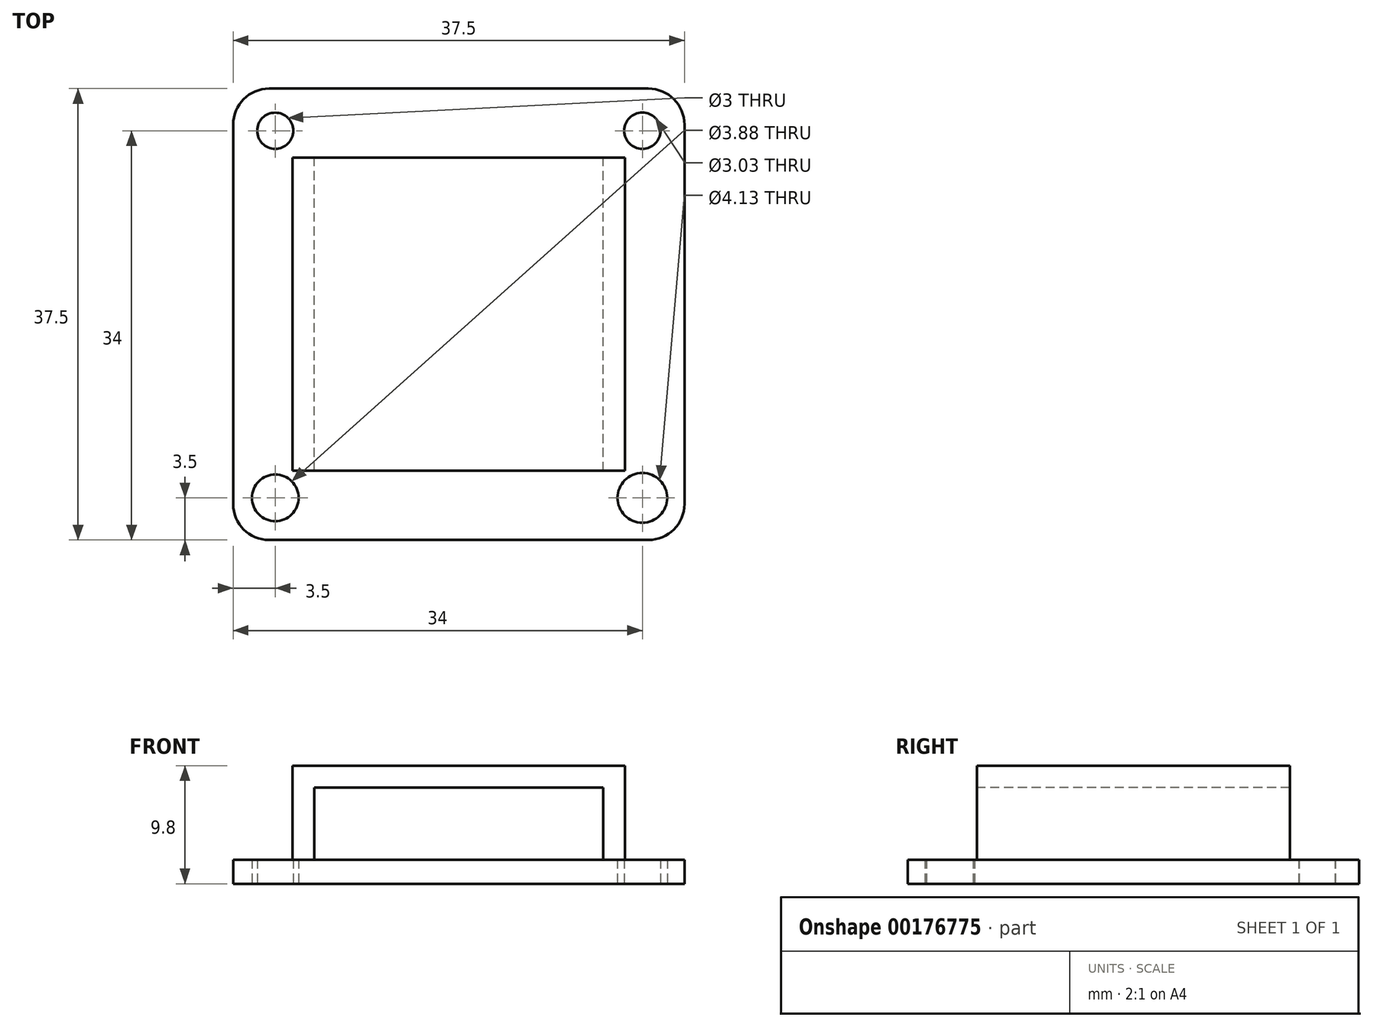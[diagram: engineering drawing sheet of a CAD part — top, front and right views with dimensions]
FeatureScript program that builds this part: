
annotation { "Feature Type Name" : "Feature", "Feature Type Description" : "" }
export const myFeature = defineFeature(function(context is Context, id is Id, definition is map)
    precondition{}
    {
        {
            var Q0;
            Q0=qCreatedBy(makeId("Top.planeOp"),FACE);
            var sketch = newSketch(context, id + "F0", { "sketchPlane" : qUnion([Q0])});
            skLineSegment(sketch, "E0.bottom", {"start": v(-15.75, 18.75) * mm, "end": v(15.75, 18.75) * mm});
            skLineSegment(sketch, "E0.top", {"start": v(-15.75, -18.75) * mm, "end": v(15.75, -18.75) * mm});
            skLineSegment(sketch, "E0.left", {"start": v(-18.75, 15.75) * mm, "end": v(-18.75, -15.75) * mm});
            skLineSegment(sketch, "E0.right", {"start": v(18.75, 15.75) * mm, "end": v(18.75, -15.75) * mm});
            skPoint(sketch, "E0.middle", {"position": v(0, 0) * mm});
            skLineSegment(sketch, "E1.bottom", {"start": v(-15.25, 15.25) * mm, "end": v(15.25, 15.25) * mm});
            skLineSegment(sketch, "E1.top", {"start": v(-15.25, -15.25) * mm, "end": v(15.25, -15.25) * mm});
            skLineSegment(sketch, "E1.left", {"start": v(-15.25, 15.25) * mm, "end": v(-15.25, -15.25) * mm});
            skLineSegment(sketch, "E1.right", {"start": v(15.25, 15.25) * mm, "end": v(15.25, -15.25) * mm});
            skCircle(sketch, "E2", {"center": v(-15.25, 15.25) * mm, "radius": 1.5 * mm});
            skCircle(sketch, "E3", {"center": v(15.25, 15.25) * mm, "radius": 1.52 * mm});
            skCircle(sketch, "E4", {"center": v(15.25, -15.25) * mm, "radius": 2.07 * mm});
            skCircle(sketch, "E5", {"center": v(-15.25, -15.25) * mm, "radius": 1.94 * mm});
            skPoint(sketch, "E6.visualSharp", {"position": v(-18.75, 18.75) * mm});
            skArc(sketch, "E6.filletArc", {"start": v(-15.75, 18.75) * mm, "mid": v(-17.87, 17.87) * mm, "end": v(-18.75, 15.75) * mm});
            skPoint(sketch, "E7.visualSharp", {"position": v(18.75, 18.75) * mm});
            skArc(sketch, "E7.filletArc", {"start": v(18.75, 15.75) * mm, "mid": v(17.87, 17.87) * mm, "end": v(15.75, 18.75) * mm});
            skPoint(sketch, "E8.visualSharp", {"position": v(18.75, -18.75) * mm});
            skArc(sketch, "E8.filletArc", {"start": v(15.75, -18.75) * mm, "mid": v(17.87, -17.87) * mm, "end": v(18.75, -15.75) * mm});
            skPoint(sketch, "E9.visualSharp", {"position": v(-18.75, -18.75) * mm});
            skArc(sketch, "E9.filletArc", {"start": v(-18.75, -15.75) * mm, "mid": v(-17.87, -17.87) * mm, "end": v(-15.75, -18.75) * mm});
            skSolve(sketch);
        }
        {
            var Q0;
            Q0 = qSketchRegion(id + "F0", true);
            var Q1;
            {var subQ5=sQuery(id+"F0.wireOp",EDGE,"E1.bottom");var subQ7=sQuery(id+"F0.wireOp",EDGE,"E2");var subQ15=makeQuery(id+"F0.imprint","INTERSECT",VERTEX,{"derivedFrom":[subQ5,subQ7]});Q1=makeQuery(id+"F0.imprint","IMPRINT",FACE,{"disambiguationData":[TD([[makeQuery(id+"F0.imprint","IMPRINT",EDGE,{"disambiguationData":[TD([[subQ15,-1.0]])],"derivedFrom":subQ5}),-1.0]])]});}
            extrude(context, id + "F1", {"entities" : qUnion([Q0, Q1]), "depth" : 2 * mm});
        }
        {
            var Q0;
            Q0=qCreatedBy(makeId("Top.planeOp"),FACE);
            var sketch = newSketch(context, id + "F2", { "sketchPlane" : qUnion([Q0])});
            skLineSegment(sketch, "E10.bottom", {"start": v(-13.8, 13) * mm, "end": v(-12, 13) * mm});
            skLineSegment(sketch, "E10.top", {"start": v(-13.8, -13) * mm, "end": v(-12, -13) * mm});
            skLineSegment(sketch, "E10.left", {"start": v(-13.8, 13) * mm, "end": v(-13.8, -13) * mm});
            skLineSegment(sketch, "E10.right", {"start": v(-12, 13) * mm, "end": v(-12, -13) * mm});
            skPoint(sketch, "E10.middle", {"position": v(-12.9, 0) * mm});
            skLineSegment(sketch, "E11.MirrorCS", {"start": v(12, 13) * mm, "end": v(12, -13) * mm});
            skLineSegment(sketch, "E12.MirrorCS", {"start": v(13.8, 13) * mm, "end": v(12, 13) * mm});
            skLineSegment(sketch, "E13.MirrorCS", {"start": v(13.8, 13) * mm, "end": v(13.8, -13) * mm});
            skLineSegment(sketch, "E14.MirrorCS", {"start": v(13.8, -13) * mm, "end": v(12, -13) * mm});
            skSolve(sketch);
        }
        {
            var Q0;
            Q0 = qSketchRegion(id + "F2", true);
            extrude(context, id + "F3", {"entities" : qUnion([Q0]), "operationType" : NewBodyOperationType.ADD, "depth" : 8 * mm});
        }
        {
            var Q0;
            Q0=makeQuery(id+"F3.opExtrude","CAP_FACE",FACE,{"disambiguationData":[OSD([sQuery(id+"F2.wireOp",EDGE,"E10.bottom"),sQuery(id+"F2.wireOp",EDGE,"E10.top"),sQuery(id+"F2.wireOp",EDGE,"E10.left"),sQuery(id+"F2.wireOp",EDGE,"E10.right")])],"isStart":false});
            var sketch = newSketch(context, id + "F4", { "sketchPlane" : qUnion([Q0])});
            skLineSegment(sketch, "E15.bottom", {"start": v(-13.8, 13) * mm, "end": v(13.8, 13) * mm});
            skLineSegment(sketch, "E15.top", {"start": v(-13.8, -13) * mm, "end": v(13.8, -13) * mm});
            skLineSegment(sketch, "E15.left", {"start": v(-13.8, 13) * mm, "end": v(-13.8, -13) * mm});
            skLineSegment(sketch, "E15.right", {"start": v(13.8, 13) * mm, "end": v(13.8, -13) * mm});
            skPoint(sketch, "E15.middle", {"position": v(0, 0) * mm});
            skSolve(sketch);
        }
        {
            var Q0;
            Q0 = qSketchRegion(id + "F4", true);
            extrude(context, id + "F5", {"entities" : qUnion([Q0]), "operationType" : NewBodyOperationType.ADD, "depth" : 1.8 * mm});
        }
    });
